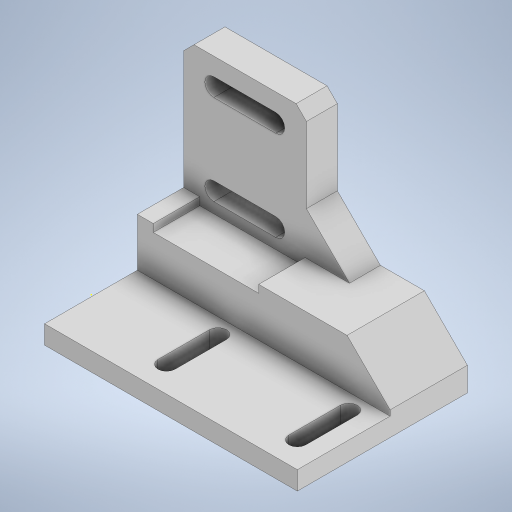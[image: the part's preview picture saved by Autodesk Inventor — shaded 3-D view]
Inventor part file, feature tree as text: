
AUTODESK INVENTOR PART (.ipt)
format: ipt  version: 2024 (Build 280153020, 153B)  size: 361,984 bytes
history: native  units: in
note: dims shown in document units (in); Inventor stores cm internally (conversion verified against a paired STEP export)
features: sketch x12, extrude x10, chamfer x3, projected_geometry x2
ambient origin geometry x8: Origin, YZ Plane, XZ Plane, XY Plane, X Axis, Y Axis, Z Axis, Center Point
bodies: Solid1 (feature_tree)
feature tree (27):
  extrude  "Extrusion1"  Depth=1.063in
  extrude  "Extrusion2"  Depth=0.2362in
  extrude  "Extrusion3"  Depth=1.4961in TaperAngle=0.0deg
  sketch  "Sketch4"  dims[d8=0.1969in d9=0.1969in]
  extrude  "Extrusion6"  Depth=0.1969in
  extrude  "Extrusion8"  Depth=1.0in
  sketch  "Sketch10"  dims[d31=0.4724in d32=0.4724in]
  extrude  "Extrusion7"  Depth=0.3937in
  extrude  "Extrusion9"  Depth=0.2976in
  extrude  "Extrusion5"  Depth=0.689in
  extrude  "Extrusion10"  Depth=0.4724in
  chamfer  "Chamfer5"  Distance=1.405in
  extrude  "Extrusion11"  Depth=0.7087in
  chamfer  "Chamfer6"  Distance=0.4724in
  chamfer  "Chamfer7"  Distance=0.3937in
  sketch  "Sketch1"  dims[d0=0.5118in d1=1.063in]
  sketch  "Sketch2"  dims[d2=1.5748in d3=0.0in d4=0.2362in]
  sketch  "Sketch3"  dims[d5=1.4961in d6=1.5748in d7=0.0in]
  sketch  "Sketch6"  dims[d10=0.3937in d11=1.0in]
  sketch  "Sketch7"  dims[d12=0.1299in d13=0.1969in d14=0.3937in d15=1.0in d16=0.1299in]
  sketch  "Sketch8"  dims[d17=1.5748in d18=0.0in d28=0.2976in]
  sketch  "Sketch9"  dims[d29=0.689in d30=0.1575in]
  sketch  "Sketch11"  dims[d33=0.1378in]
  projected_geometry  "Projected Loop1"
  sketch  "Sketch13"  dims[d34=0.1378in d35=1.405in d36=0.0in]
  sketch  "Sketch14"  dims[d37=1.7825in d38=0.0in d53=0.0984in d54=0.4724in d55=0.3937in d56=0.0591in d57=0.0in d58=0.1417in d59=0.7087in d60=1.9813in d61=0.0in d62=0.3563in d63=0.0in d64=0.3563in d65=0.0in d66=0.3287in d67=0.0787in d68=45.0deg d69=0.2062in d70=0.0in d71=0.3287in d72=0.0787in d73=45.0deg d74=0.0787in d75=0.0787in d76=45.0deg]
  projected_geometry  "Projected Loop2"
